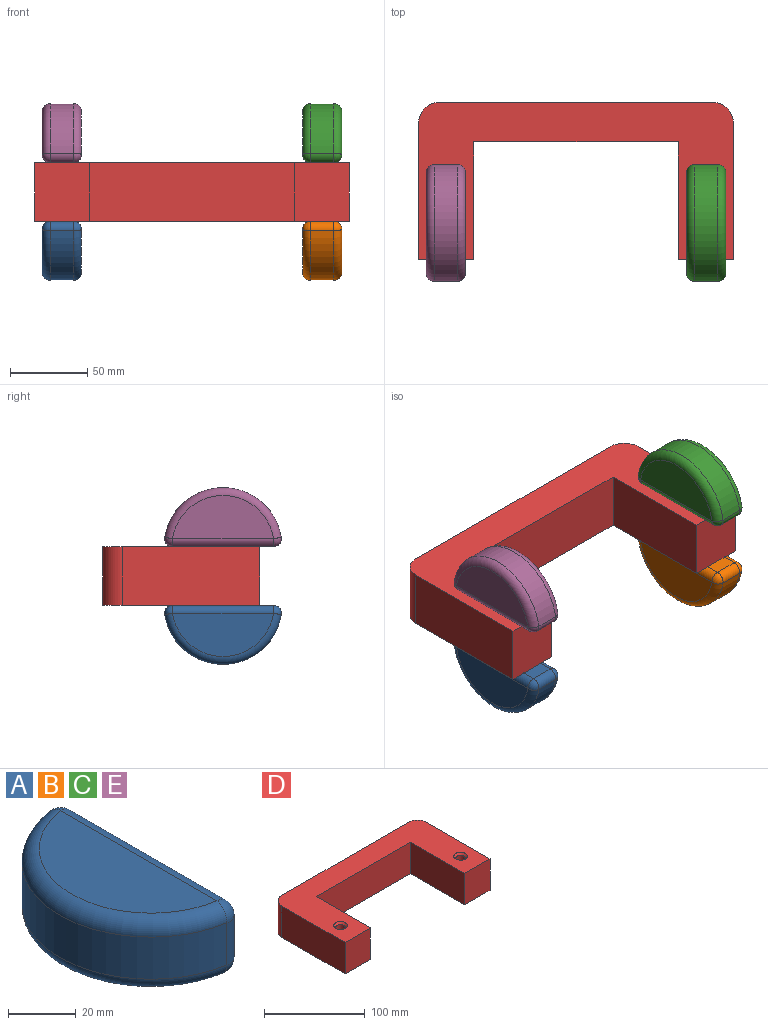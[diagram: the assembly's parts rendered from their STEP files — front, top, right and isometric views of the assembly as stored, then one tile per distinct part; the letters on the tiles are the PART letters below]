
ASSEMBLY  parts=5 mates=4
PART A: 14 faces, bbox 41.2x81.5x25.4 mm
  f0: cylinder r=38.1mm len=75.29mm, axis (0,0,-1), area 1644.8mm2, adj f4,f8,f9,f13
  f1: plane 65.25x27.94mm, normal (0,0,1), area 1378.5mm2, adj f7,f8
  f2: plane 65.25x27.94mm, normal (0,0,-1), area 1378.5mm2, adj f9,f10
  f3: plane 65.25x15.24mm, normal (1,0,0), area 994.5mm2, adj f4,f7,f10,f13
  f4: cylinder r=5.08mm len=15.24mm, axis (0,0,-1), area 133.6mm2, adj f0,f3,f5,f6
  f5: sphere r=5.08mm, area 44.5mm2, adj f4,f7,f8
  f6: sphere r=5.08mm, area 44.5mm2, adj f4,f9,f10
  f7: cylinder r=5.08mm len=65.25mm, axis (0,1,0), area 520.7mm2, adj f1,f3,f5,f11
  f8: torus R=33.02mm, axis (0,0,1), area 819.5mm2, adj f0,f1,f5,f11
  f9: torus R=33.02mm, axis (0,0,1), area 819.5mm2, adj f0,f2,f6,f12
  f10: cylinder r=5.08mm len=65.25mm, axis (0,-1,0), area 520.7mm2, adj f2,f3,f6,f12
  f11: sphere r=5.08mm, area 44.5mm2, adj f7,f8,f13
  f12: sphere r=5.08mm, area 44.5mm2, adj f9,f10,f13
  f13: cylinder r=5.08mm len=15.24mm, axis (0,0,-1), area 133.6mm2, adj f0,f3,f11,f12
PART B: same geometry as A
PART C: same geometry as A
PART D: 16 faces, bbox 203.2x101.6x38.1 mm
  f0: plane 88.9x38.1mm, normal (-1,0,0), area 3387.1mm2, adj f1,f9,f10,f11
  f1: plane 38.1x35.56mm, normal (0,-1,0), area 1354.8mm2, adj f0,f2,f10,f11
  f2: plane 76.2x38.1mm, normal (1,0,0), area 2903.2mm2, adj f1,f3,f10,f11
  f3: plane 132.08x38.1mm, normal (0,-1,0), area 5032.2mm2, adj f2,f4,f10,f11
  f4: plane 76.2x38.1mm, normal (-1,0,0), area 2903.2mm2, adj f3,f5,f10,f11
  f5: plane 38.1x35.56mm, normal (0,-1,0), area 1354.8mm2, adj f4,f6,f10,f11
  f6: plane 88.9x38.1mm, normal (1,0,0), area 3387.1mm2, adj f5,f7,f10,f11
  f7: cylinder r=12.7mm len=38.1mm, axis (0,0,-1), area 760.1mm2, adj f6,f8,f10,f11
  f8: plane 177.8x38.1mm, normal (0,1,0), area 6774.2mm2, adj f7,f9,f10,f11
  f9: cylinder r=12.7mm len=38.1mm, axis (0,0,-1), area 760.1mm2, adj f0,f8,f10,f11
  f10: plane 203.2x101.6mm, normal (0,0,1), area 10225.7mm2, adj f0,f1,f2,f3,f4,f5,f6,f7
  f11: plane 203.2x101.6mm, normal (0,0,-1), area 10368.9mm2, adj f0,f1,f2,f3,f4,f5,f6,f7
  f12: cylinder r=4.76mm len=35.82mm, axis (0,0,1), area 1071.9mm2, adj f11,f13
  f13: cone r=4.76mm half-angle=41deg, axis (0,0,1), area 109.2mm2, adj f10,f12
  f14: cylinder r=4.76mm len=35.82mm, axis (0,0,1), area 1071.9mm2, adj f11,f15
  f15: cone r=4.76mm half-angle=41deg, axis (0,0,1), area 109.2mm2, adj f10,f14
PART E: same geometry as A
PLACE A rot(axis=(0.71,0,0.71),180deg) t=(-83.39,-29.71,-27.64)mm
PLACE B rot(axis=(0.71,0,0.71),180deg) t=(84.89,-29.71,-27.64)mm
PLACE C rot(axis=(0.71,0,-0.71),180deg) t=(110.29,-29.71,10.46)mm
PLACE D t=(4.81,-10.65,-27.64)mm
PLACE E rot(axis=(0.71,0,-0.71),180deg) t=(-57.99,-29.71,10.46)mm
MATE fastened E.f3 <-> D.f12  axis (0,0,-1) through (-70.69,-29.71,10.46)mm
MATE fastened A.f3 <-> D.f12  axis (0,0,1) through (-70.69,-29.71,-27.64)mm
MATE fastened C.f3 <-> D.f14  axis (0,0,-1) through (97.59,-29.71,10.46)mm
MATE fastened B.f3 <-> D.f14  axis (0,0,1) through (97.59,-29.71,-27.64)mm
